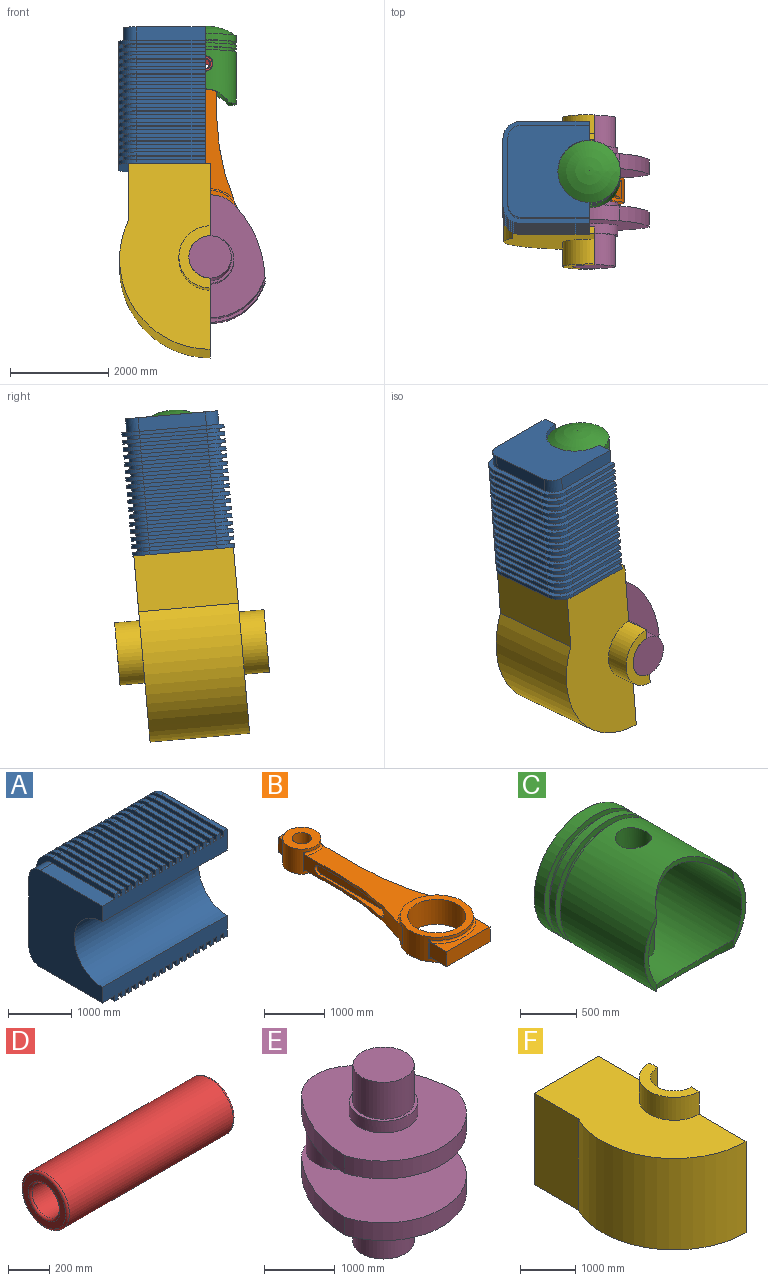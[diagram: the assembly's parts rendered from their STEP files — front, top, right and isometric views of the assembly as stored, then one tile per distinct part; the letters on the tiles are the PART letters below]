
ASSEMBLY  parts=6 mates=6
PART A: 208 faces, bbox 2794x1752.6x2082.8 mm
  f0: plane 1397x279.4mm, normal (0,0,-1), area 390321.8mm2, adj f1,f86,f89,f206
  f1: cylinder r=254mm len=279.4mm, axis (-1,0,0), area 111475.6mm2, adj f0,f2,f89,f206
  f2: plane 1371.6x279.4mm, normal (0,1,0), area 383225mm2, adj f1,f3,f89,f206
  f3: cylinder r=254mm len=279.4mm, axis (-1,0,0), area 111475.6mm2, adj f2,f4,f89,f206
  f4: plane 1397x279.4mm, normal (0,0,1), area 390321.8mm2, adj f3,f87,f89,f206
  f5: plane 1397x76.2mm, normal (0,0,-1), area 106451.4mm2, adj f6,f86,f199,f207
  f6: cylinder r=254mm len=254mm, axis (-1,0,0), area 30402.4mm2, adj f5,f7,f199,f207
  f7: plane 1371.6x76.2mm, normal (0,1,0), area 104515.9mm2, adj f6,f8,f199,f207
  f8: cylinder r=254mm len=254mm, axis (-1,0,0), area 30402.4mm2, adj f7,f9,f199,f207
  f9: plane 1397x76.2mm, normal (0,0,1), area 106451.4mm2, adj f8,f87,f199,f207
  f10: plane 1397x76.2mm, normal (0,0,-1), area 106451.4mm2, adj f11,f86,f192,f200
  f11: cylinder r=254mm len=254mm, axis (-1,0,0), area 30402.4mm2, adj f10,f12,f192,f200
  f12: plane 1371.6x76.2mm, normal (0,1,0), area 104515.9mm2, adj f11,f13,f192,f200
  f13: cylinder r=254mm len=254mm, axis (-1,0,0), area 30402.4mm2, adj f12,f14,f192,f200
  f14: plane 1397x76.2mm, normal (0,0,1), area 106451.4mm2, adj f13,f87,f192,f200
  f15: plane 1397x76.2mm, normal (0,0,-1), area 106451.4mm2, adj f16,f86,f185,f193
  f16: cylinder r=254mm len=254mm, axis (-1,0,0), area 30402.4mm2, adj f15,f17,f185,f193
  f17: plane 1371.6x76.2mm, normal (0,1,0), area 104515.9mm2, adj f16,f18,f185,f193
  f18: cylinder r=254mm len=254mm, axis (-1,0,0), area 30402.4mm2, adj f17,f19,f185,f193
  f19: plane 1397x76.2mm, normal (0,0,1), area 106451.4mm2, adj f18,f87,f185,f193
  f20: plane 1397x76.2mm, normal (0,0,-1), area 106451.4mm2, adj f21,f86,f178,f186
  f21: cylinder r=254mm len=254mm, axis (-1,0,0), area 30402.4mm2, adj f20,f22,f178,f186
  f22: plane 1371.6x76.2mm, normal (0,1,0), area 104515.9mm2, adj f21,f23,f178,f186
  f23: cylinder r=254mm len=254mm, axis (-1,0,0), area 30402.4mm2, adj f22,f24,f178,f186
  f24: plane 1397x76.2mm, normal (0,0,1), area 106451.4mm2, adj f23,f87,f178,f186
  f25: plane 1397x76.2mm, normal (0,0,-1), area 106451.4mm2, adj f26,f86,f171,f179
  f26: cylinder r=254mm len=254mm, axis (-1,0,0), area 30402.4mm2, adj f25,f27,f171,f179
  f27: plane 1371.6x76.2mm, normal (0,1,0), area 104515.9mm2, adj f26,f28,f171,f179
  f28: cylinder r=254mm len=254mm, axis (-1,0,0), area 30402.4mm2, adj f27,f29,f171,f179
  f29: plane 1397x76.2mm, normal (0,0,1), area 106451.4mm2, adj f28,f87,f171,f179
  f30: plane 1397x76.2mm, normal (0,0,-1), area 106451.4mm2, adj f31,f86,f164,f172
  f31: cylinder r=254mm len=254mm, axis (-1,0,0), area 30402.4mm2, adj f30,f32,f164,f172
  f32: plane 1371.6x76.2mm, normal (0,1,0), area 104515.9mm2, adj f31,f33,f164,f172
  f33: cylinder r=254mm len=254mm, axis (-1,0,0), area 30402.4mm2, adj f32,f34,f164,f172
  f34: plane 1397x76.2mm, normal (0,0,1), area 106451.4mm2, adj f33,f87,f164,f172
  f35: plane 1397x76.2mm, normal (0,0,-1), area 106451.4mm2, adj f36,f86,f157,f165
  f36: cylinder r=254mm len=254mm, axis (-1,0,0), area 30402.4mm2, adj f35,f37,f157,f165
  f37: plane 1371.6x76.2mm, normal (0,1,0), area 104515.9mm2, adj f36,f38,f157,f165
  f38: cylinder r=254mm len=254mm, axis (-1,0,0), area 30402.4mm2, adj f37,f39,f157,f165
  f39: plane 1397x76.2mm, normal (0,0,1), area 106451.4mm2, adj f38,f87,f157,f165
  f40: plane 1397x76.2mm, normal (0,0,-1), area 106451.4mm2, adj f41,f86,f150,f158
  f41: cylinder r=254mm len=254mm, axis (-1,0,0), area 30402.4mm2, adj f40,f42,f150,f158
  f42: plane 1371.6x76.2mm, normal (0,1,0), area 104515.9mm2, adj f41,f43,f150,f158
  f43: cylinder r=254mm len=254mm, axis (-1,0,0), area 30402.4mm2, adj f42,f44,f150,f158
  f44: plane 1397x76.2mm, normal (0,0,1), area 106451.4mm2, adj f43,f87,f150,f158
  f45: plane 1397x76.2mm, normal (0,0,-1), area 106451.4mm2, adj f46,f86,f143,f151
  f46: cylinder r=254mm len=254mm, axis (-1,0,0), area 30402.4mm2, adj f45,f47,f143,f151
  f47: plane 1371.6x76.2mm, normal (0,1,0), area 104515.9mm2, adj f46,f48,f143,f151
  f48: cylinder r=254mm len=254mm, axis (-1,0,0), area 30402.4mm2, adj f47,f49,f143,f151
  f49: plane 1397x76.2mm, normal (0,0,1), area 106451.4mm2, adj f48,f87,f143,f151
  f50: plane 1397x76.2mm, normal (0,0,-1), area 106451.4mm2, adj f51,f86,f136,f144
  f51: cylinder r=254mm len=254mm, axis (-1,0,0), area 30402.4mm2, adj f50,f52,f136,f144
  f52: plane 1371.6x76.2mm, normal (0,1,0), area 104515.9mm2, adj f51,f53,f136,f144
  f53: cylinder r=254mm len=254mm, axis (-1,0,0), area 30402.4mm2, adj f52,f54,f136,f144
  f54: plane 1397x76.2mm, normal (0,0,1), area 106451.4mm2, adj f53,f87,f136,f144
  f55: plane 1397x76.2mm, normal (0,0,-1), area 106451.4mm2, adj f56,f86,f129,f137
  f56: cylinder r=254mm len=254mm, axis (-1,0,0), area 30402.4mm2, adj f55,f57,f129,f137
  f57: plane 1371.6x76.2mm, normal (0,1,0), area 104515.9mm2, adj f56,f58,f129,f137
  f58: cylinder r=254mm len=254mm, axis (-1,0,0), area 30402.4mm2, adj f57,f59,f129,f137
  f59: plane 1397x76.2mm, normal (0,0,1), area 106451.4mm2, adj f58,f87,f129,f137
  f60: plane 1397x76.2mm, normal (0,0,-1), area 106451.4mm2, adj f61,f86,f122,f130
  f61: cylinder r=254mm len=254mm, axis (-1,0,0), area 30402.4mm2, adj f60,f62,f122,f130
  f62: plane 1371.6x76.2mm, normal (0,1,0), area 104515.9mm2, adj f61,f63,f122,f130
  f63: cylinder r=254mm len=254mm, axis (-1,0,0), area 30402.4mm2, adj f62,f64,f122,f130
  f64: plane 1397x76.2mm, normal (0,0,1), area 106451.4mm2, adj f63,f87,f122,f130
  f65: plane 1397x76.2mm, normal (0,0,-1), area 106451.4mm2, adj f66,f86,f115,f123
  f66: cylinder r=254mm len=254mm, axis (-1,0,0), area 30402.4mm2, adj f65,f67,f115,f123
  f67: plane 1371.6x76.2mm, normal (0,1,0), area 104515.9mm2, adj f66,f68,f115,f123
  f68: cylinder r=254mm len=254mm, axis (-1,0,0), area 30402.4mm2, adj f67,f69,f115,f123
  f69: plane 1397x76.2mm, normal (0,0,1), area 106451.4mm2, adj f68,f87,f115,f123
  f70: plane 1397x76.2mm, normal (0,0,-1), area 106451.4mm2, adj f71,f86,f108,f116
  f71: cylinder r=254mm len=254mm, axis (-1,0,0), area 30402.4mm2, adj f70,f72,f108,f116
  f72: plane 1371.6x76.2mm, normal (0,1,0), area 104515.9mm2, adj f71,f73,f108,f116
  f73: cylinder r=254mm len=254mm, axis (-1,0,0), area 30402.4mm2, adj f72,f74,f108,f116
  f74: plane 1397x76.2mm, normal (0,0,1), area 106451.4mm2, adj f73,f87,f108,f116
  f75: plane 1397x76.2mm, normal (0,0,-1), area 106451.4mm2, adj f76,f86,f101,f109
  f76: cylinder r=254mm len=254mm, axis (-1,0,0), area 30402.4mm2, adj f75,f77,f101,f109
  f77: plane 1371.6x76.2mm, normal (0,1,0), area 104515.9mm2, adj f76,f78,f101,f109
  f78: cylinder r=254mm len=254mm, axis (-1,0,0), area 30402.4mm2, adj f77,f79,f101,f109
  f79: plane 1397x76.2mm, normal (0,0,1), area 106451.4mm2, adj f78,f87,f101,f109
  f80: plane 1397x76.2mm, normal (0,0,-1), area 106451.4mm2, adj f81,f86,f95,f102
  f81: cylinder r=254mm len=254mm, axis (-1,0,0), area 30402.4mm2, adj f80,f82,f95,f102
  f82: plane 1371.6x76.2mm, normal (0,1,0), area 104515.9mm2, adj f81,f83,f95,f102
  f83: cylinder r=254mm len=254mm, axis (-1,0,0), area 30402.4mm2, adj f82,f84,f95,f102
  f84: plane 1397x76.2mm, normal (0,0,1), area 106451.4mm2, adj f83,f87,f95,f102
  f85: cylinder r=635mm len=2794mm, axis (-1,0,0), area 5573782.3mm2, adj f86,f87,f88,f89
  f86: plane 2794x406.4mm, normal (0,-1,0), area 983223.8mm2, adj f0,f5,f10,f15,f20,f25,f30,f35
  f87: plane 2794x406.4mm, normal (0,-1,0), area 983223.8mm2, adj f4,f9,f14,f19,f24,f29,f34,f39
  f88: plane 2082.8x1752.6mm, normal (1,0,0), area 2962657.5mm2, adj f85,f86,f87,f90,f91,f92,f93,f94
  f89: plane 1879.6x1651mm, normal (-1,0,0), area 2442144.7mm2, adj f0,f1,f2,f3,f4,f85,f86,f87
  f90: plane 1397x76.2mm, normal (0,0,-1), area 106451.4mm2, adj f86,f88,f94,f95
  f91: plane 1397x76.2mm, normal (0,0,1), area 106451.4mm2, adj f87,f88,f92,f95
  f92: cylinder r=355.6mm len=355.6mm, axis (1,0,0), area 42563.4mm2, adj f88,f91,f93,f95
  f93: plane 1371.6x76.2mm, normal (0,1,0), area 104515.9mm2, adj f88,f92,f94,f95
  f94: cylinder r=355.6mm len=355.6mm, axis (1,0,0), area 42563.4mm2, adj f88,f90,f93,f95
  f95: plane 2082.8x1752.6mm, normal (-1,0,0), area 520512.8mm2, adj f80,f81,f82,f83,f84,f86,f87,f90
  f96: plane 1397x76.2mm, normal (0,0,-1), area 106451.4mm2, adj f86,f100,f101,f102
  f97: plane 1397x76.2mm, normal (0,0,1), area 106451.4mm2, adj f87,f98,f101,f102
  f98: cylinder r=355.6mm len=355.6mm, axis (1,0,0), area 42563.4mm2, adj f97,f99,f101,f102
  f99: plane 1371.6x76.2mm, normal (0,1,0), area 104515.9mm2, adj f98,f100,f101,f102
  f100: cylinder r=355.6mm len=355.6mm, axis (1,0,0), area 42563.4mm2, adj f96,f99,f101,f102
  f101: plane 2082.8x1752.6mm, normal (-1,0,0), area 520512.8mm2, adj f75,f76,f77,f78,f79,f86,f87,f96
  f102: plane 2082.8x1752.6mm, normal (1,0,0), area 520512.8mm2, adj f80,f81,f82,f83,f84,f86,f87,f96
  f103: plane 1397x76.2mm, normal (0,0,-1), area 106451.4mm2, adj f86,f107,f108,f109
  f104: plane 1397x76.2mm, normal (0,0,1), area 106451.4mm2, adj f87,f105,f108,f109
  f105: cylinder r=355.6mm len=355.6mm, axis (1,0,0), area 42563.4mm2, adj f104,f106,f108,f109
  f106: plane 1371.6x76.2mm, normal (0,1,0), area 104515.9mm2, adj f105,f107,f108,f109
  f107: cylinder r=355.6mm len=355.6mm, axis (1,0,0), area 42563.4mm2, adj f103,f106,f108,f109
  f108: plane 2082.8x1752.6mm, normal (-1,0,0), area 520512.8mm2, adj f70,f71,f72,f73,f74,f86,f87,f103
  f109: plane 2082.8x1752.6mm, normal (1,0,0), area 520512.8mm2, adj f75,f76,f77,f78,f79,f86,f87,f103
  f110: plane 1397x76.2mm, normal (0,0,-1), area 106451.4mm2, adj f86,f114,f115,f116
  f111: plane 1397x76.2mm, normal (0,0,1), area 106451.4mm2, adj f87,f112,f115,f116
  f112: cylinder r=355.6mm len=355.6mm, axis (1,0,0), area 42563.4mm2, adj f111,f113,f115,f116
  f113: plane 1371.6x76.2mm, normal (0,1,0), area 104515.9mm2, adj f112,f114,f115,f116
  f114: cylinder r=355.6mm len=355.6mm, axis (1,0,0), area 42563.4mm2, adj f110,f113,f115,f116
  f115: plane 2082.8x1752.6mm, normal (-1,0,0), area 520512.8mm2, adj f65,f66,f67,f68,f69,f86,f87,f110
  f116: plane 2082.8x1752.6mm, normal (1,0,0), area 520512.8mm2, adj f70,f71,f72,f73,f74,f86,f87,f110
  f117: plane 1397x76.2mm, normal (0,0,-1), area 106451.4mm2, adj f86,f121,f122,f123
  f118: plane 1397x76.2mm, normal (0,0,1), area 106451.4mm2, adj f87,f119,f122,f123
  f119: cylinder r=355.6mm len=355.6mm, axis (1,0,0), area 42563.4mm2, adj f118,f120,f122,f123
  f120: plane 1371.6x76.2mm, normal (0,1,0), area 104515.9mm2, adj f119,f121,f122,f123
  f121: cylinder r=355.6mm len=355.6mm, axis (1,0,0), area 42563.4mm2, adj f117,f120,f122,f123
  f122: plane 2082.8x1752.6mm, normal (-1,0,0), area 520512.8mm2, adj f60,f61,f62,f63,f64,f86,f87,f117
  f123: plane 2082.8x1752.6mm, normal (1,0,0), area 520512.8mm2, adj f65,f66,f67,f68,f69,f86,f87,f117
  f124: plane 1397x76.2mm, normal (0,0,-1), area 106451.4mm2, adj f86,f128,f129,f130
  f125: plane 1397x76.2mm, normal (0,0,1), area 106451.4mm2, adj f87,f126,f129,f130
  f126: cylinder r=355.6mm len=355.6mm, axis (1,0,0), area 42563.4mm2, adj f125,f127,f129,f130
  f127: plane 1371.6x76.2mm, normal (0,1,0), area 104515.9mm2, adj f126,f128,f129,f130
  f128: cylinder r=355.6mm len=355.6mm, axis (1,0,0), area 42563.4mm2, adj f124,f127,f129,f130
  f129: plane 2082.8x1752.6mm, normal (-1,0,0), area 520512.8mm2, adj f55,f56,f57,f58,f59,f86,f87,f124
  f130: plane 2082.8x1752.6mm, normal (1,0,0), area 520512.8mm2, adj f60,f61,f62,f63,f64,f86,f87,f124
  f131: plane 1397x76.2mm, normal (0,0,-1), area 106451.4mm2, adj f86,f135,f136,f137
  f132: plane 1397x76.2mm, normal (0,0,1), area 106451.4mm2, adj f87,f133,f136,f137
  f133: cylinder r=355.6mm len=355.6mm, axis (1,0,0), area 42563.4mm2, adj f132,f134,f136,f137
  f134: plane 1371.6x76.2mm, normal (0,1,0), area 104515.9mm2, adj f133,f135,f136,f137
  f135: cylinder r=355.6mm len=355.6mm, axis (1,0,0), area 42563.4mm2, adj f131,f134,f136,f137
  f136: plane 2082.8x1752.6mm, normal (-1,0,0), area 520512.8mm2, adj f50,f51,f52,f53,f54,f86,f87,f131
  f137: plane 2082.8x1752.6mm, normal (1,0,0), area 520512.8mm2, adj f55,f56,f57,f58,f59,f86,f87,f131
  f138: plane 1397x76.2mm, normal (0,0,-1), area 106451.4mm2, adj f86,f142,f143,f144
  f139: plane 1397x76.2mm, normal (0,0,1), area 106451.4mm2, adj f87,f140,f143,f144
  f140: cylinder r=355.6mm len=355.6mm, axis (1,0,0), area 42563.4mm2, adj f139,f141,f143,f144
  f141: plane 1371.6x76.2mm, normal (0,1,0), area 104515.9mm2, adj f140,f142,f143,f144
  f142: cylinder r=355.6mm len=355.6mm, axis (1,0,0), area 42563.4mm2, adj f138,f141,f143,f144
  f143: plane 2082.8x1752.6mm, normal (-1,0,0), area 520512.8mm2, adj f45,f46,f47,f48,f49,f86,f87,f138
  f144: plane 2082.8x1752.6mm, normal (1,0,0), area 520512.8mm2, adj f50,f51,f52,f53,f54,f86,f87,f138
  f145: plane 1397x76.2mm, normal (0,0,-1), area 106451.4mm2, adj f86,f149,f150,f151
  f146: plane 1397x76.2mm, normal (0,0,1), area 106451.4mm2, adj f87,f147,f150,f151
  f147: cylinder r=355.6mm len=355.6mm, axis (1,0,0), area 42563.4mm2, adj f146,f148,f150,f151
  f148: plane 1371.6x76.2mm, normal (0,1,0), area 104515.9mm2, adj f147,f149,f150,f151
  f149: cylinder r=355.6mm len=355.6mm, axis (1,0,0), area 42563.4mm2, adj f145,f148,f150,f151
  f150: plane 2082.8x1752.6mm, normal (-1,0,0), area 520512.8mm2, adj f40,f41,f42,f43,f44,f86,f87,f145
  f151: plane 2082.8x1752.6mm, normal (1,0,0), area 520512.8mm2, adj f45,f46,f47,f48,f49,f86,f87,f145
  f152: plane 1397x76.2mm, normal (0,0,-1), area 106451.4mm2, adj f86,f156,f157,f158
  f153: plane 1397x76.2mm, normal (0,0,1), area 106451.4mm2, adj f87,f154,f157,f158
  f154: cylinder r=355.6mm len=355.6mm, axis (1,0,0), area 42563.4mm2, adj f153,f155,f157,f158
  f155: plane 1371.6x76.2mm, normal (0,1,0), area 104515.9mm2, adj f154,f156,f157,f158
  f156: cylinder r=355.6mm len=355.6mm, axis (1,0,0), area 42563.4mm2, adj f152,f155,f157,f158
  f157: plane 2082.8x1752.6mm, normal (-1,0,0), area 520512.8mm2, adj f35,f36,f37,f38,f39,f86,f87,f152
  f158: plane 2082.8x1752.6mm, normal (1,0,0), area 520512.8mm2, adj f40,f41,f42,f43,f44,f86,f87,f152
  f159: plane 1397x76.2mm, normal (0,0,-1), area 106451.4mm2, adj f86,f163,f164,f165
  f160: plane 1397x76.2mm, normal (0,0,1), area 106451.4mm2, adj f87,f161,f164,f165
  f161: cylinder r=355.6mm len=355.6mm, axis (1,0,0), area 42563.4mm2, adj f160,f162,f164,f165
  f162: plane 1371.6x76.2mm, normal (0,1,0), area 104515.9mm2, adj f161,f163,f164,f165
  f163: cylinder r=355.6mm len=355.6mm, axis (1,0,0), area 42563.4mm2, adj f159,f162,f164,f165
  f164: plane 2082.8x1752.6mm, normal (-1,0,0), area 520512.8mm2, adj f30,f31,f32,f33,f34,f86,f87,f159
  f165: plane 2082.8x1752.6mm, normal (1,0,0), area 520512.8mm2, adj f35,f36,f37,f38,f39,f86,f87,f159
  f166: plane 1397x76.2mm, normal (0,0,-1), area 106451.4mm2, adj f86,f170,f171,f172
  f167: plane 1397x76.2mm, normal (0,0,1), area 106451.4mm2, adj f87,f168,f171,f172
  f168: cylinder r=355.6mm len=355.6mm, axis (1,0,0), area 42563.4mm2, adj f167,f169,f171,f172
  f169: plane 1371.6x76.2mm, normal (0,1,0), area 104515.9mm2, adj f168,f170,f171,f172
  f170: cylinder r=355.6mm len=355.6mm, axis (1,0,0), area 42563.4mm2, adj f166,f169,f171,f172
  f171: plane 2082.8x1752.6mm, normal (-1,0,0), area 520512.8mm2, adj f25,f26,f27,f28,f29,f86,f87,f166
  f172: plane 2082.8x1752.6mm, normal (1,0,0), area 520512.8mm2, adj f30,f31,f32,f33,f34,f86,f87,f166
  f173: plane 1397x76.2mm, normal (0,0,-1), area 106451.4mm2, adj f86,f177,f178,f179
  f174: plane 1397x76.2mm, normal (0,0,1), area 106451.4mm2, adj f87,f175,f178,f179
  f175: cylinder r=355.6mm len=355.6mm, axis (1,0,0), area 42563.4mm2, adj f174,f176,f178,f179
  f176: plane 1371.6x76.2mm, normal (0,1,0), area 104515.9mm2, adj f175,f177,f178,f179
  f177: cylinder r=355.6mm len=355.6mm, axis (1,0,0), area 42563.4mm2, adj f173,f176,f178,f179
  f178: plane 2082.8x1752.6mm, normal (-1,0,0), area 520512.8mm2, adj f20,f21,f22,f23,f24,f86,f87,f173
  f179: plane 2082.8x1752.6mm, normal (1,0,0), area 520512.8mm2, adj f25,f26,f27,f28,f29,f86,f87,f173
  f180: plane 1397x76.2mm, normal (0,0,-1), area 106451.4mm2, adj f86,f184,f185,f186
  f181: plane 1397x76.2mm, normal (0,0,1), area 106451.4mm2, adj f87,f182,f185,f186
  f182: cylinder r=355.6mm len=355.6mm, axis (1,0,0), area 42563.4mm2, adj f181,f183,f185,f186
  f183: plane 1371.6x76.2mm, normal (0,1,0), area 104515.9mm2, adj f182,f184,f185,f186
  f184: cylinder r=355.6mm len=355.6mm, axis (1,0,0), area 42563.4mm2, adj f180,f183,f185,f186
  f185: plane 2082.8x1752.6mm, normal (-1,0,0), area 520512.8mm2, adj f15,f16,f17,f18,f19,f86,f87,f180
  f186: plane 2082.8x1752.6mm, normal (1,0,0), area 520512.8mm2, adj f20,f21,f22,f23,f24,f86,f87,f180
  f187: plane 1397x76.2mm, normal (0,0,-1), area 106451.4mm2, adj f86,f191,f192,f193
  f188: plane 1397x76.2mm, normal (0,0,1), area 106451.4mm2, adj f87,f189,f192,f193
  f189: cylinder r=355.6mm len=355.6mm, axis (1,0,0), area 42563.4mm2, adj f188,f190,f192,f193
  f190: plane 1371.6x76.2mm, normal (0,1,0), area 104515.9mm2, adj f189,f191,f192,f193
  f191: cylinder r=355.6mm len=355.6mm, axis (1,0,0), area 42563.4mm2, adj f187,f190,f192,f193
  f192: plane 2082.8x1752.6mm, normal (-1,0,0), area 520512.8mm2, adj f10,f11,f12,f13,f14,f86,f87,f187
  f193: plane 2082.8x1752.6mm, normal (1,0,0), area 520512.8mm2, adj f15,f16,f17,f18,f19,f86,f87,f187
  f194: plane 1397x76.2mm, normal (0,0,-1), area 106451.4mm2, adj f86,f198,f199,f200
  f195: plane 1397x76.2mm, normal (0,0,1), area 106451.4mm2, adj f87,f196,f199,f200
  f196: cylinder r=355.6mm len=355.6mm, axis (1,0,0), area 42563.4mm2, adj f195,f197,f199,f200
  f197: plane 1371.6x76.2mm, normal (0,1,0), area 104515.9mm2, adj f196,f198,f199,f200
  f198: cylinder r=355.6mm len=355.6mm, axis (1,0,0), area 42563.4mm2, adj f194,f197,f199,f200
  f199: plane 2082.8x1752.6mm, normal (-1,0,0), area 520512.8mm2, adj f5,f6,f7,f8,f9,f86,f87,f194
  f200: plane 2082.8x1752.6mm, normal (1,0,0), area 520512.8mm2, adj f10,f11,f12,f13,f14,f86,f87,f194
  f201: plane 1397x76.2mm, normal (0,0,-1), area 106451.4mm2, adj f86,f205,f206,f207
  f202: plane 1397x76.2mm, normal (0,0,1), area 106451.4mm2, adj f87,f203,f206,f207
  f203: cylinder r=355.6mm len=355.6mm, axis (1,0,0), area 42563.4mm2, adj f202,f204,f206,f207
  f204: plane 1371.6x76.2mm, normal (0,1,0), area 104515.9mm2, adj f203,f205,f206,f207
  f205: cylinder r=355.6mm len=355.6mm, axis (1,0,0), area 42563.4mm2, adj f201,f204,f206,f207
  f206: plane 2082.8x1752.6mm, normal (-1,0,0), area 520512.8mm2, adj f0,f1,f2,f3,f4,f86,f87,f201
  f207: plane 2082.8x1752.6mm, normal (1,0,0), area 520512.8mm2, adj f5,f6,f7,f8,f9,f86,f87,f201
PART B: 46 faces, bbox 1349.2x4329.7x508.1 mm
  f0: cylinder r=4709.32mm len=1805.43mm, axis (0,0,-1), area 349864.6mm2, adj f1,f4,f8,f9,f28,f29,f36,f38
  f1: plane 889x381mm, normal (1,0,0), area 154137.5mm2, adj f0,f8,f9,f12,f30,f31,f37,f38
  f2: plane 1219.2x1219.2mm, normal (0,0,1), area 435768.4mm2, adj f4,f5
  f3: plane 1219.2x1219.2mm, normal (0,0,-1), area 435768.4mm2, adj f4,f5
  f4: cylinder r=609.6mm len=1219.2mm, axis (0,0,-1), area 932908.3mm2, adj f0,f2,f3,f7,f24,f25,f26,f27
  f5: cylinder r=482.6mm len=965.2mm, axis (0,0,-1), area 1540390.7mm2, adj f2,f3
  f6: plane 889x381mm, normal (-1,0,0), area 154138.3mm2, adj f7,f8,f9,f12,f30,f31,f41,f42
  f7: cylinder r=4709.32mm len=1805.43mm, axis (0,0,-1), area 349901.4mm2, adj f4,f6,f8,f9,f28,f29,f42,f43
  f8: plane 2454.67x976.49mm, normal (0,0,1), area 1132367.6mm2, adj f0,f1,f6,f7,f29,f30
  f9: plane 2454.67x976.49mm, normal (0,0,-1), area 1132367.6mm2, adj f0,f1,f6,f7,f28,f31
  f10: plane 635x635mm, normal (0,0,1), area 237519.1mm2, adj f12,f13
  f11: plane 635x635mm, normal (0,0,-1), area 237519.1mm2, adj f12,f13
  f12: cylinder r=317.5mm len=635mm, axis (0,0,-1), area 703461.2mm2, adj f1,f6,f10,f11,f30,f31,f32,f33
  f13: cylinder r=158.75mm len=508mm, axis (0,0,-1), area 506707.5mm2, adj f10,f11
  f14: plane 317.5x304.8mm, normal (0,1,0), area 96774mm2, adj f15,f16,f17,f18
  f15: plane 315.74x105.91mm, normal (-1,0,0), area 32331.2mm2, adj f14,f17,f18,f32,f33,f35
  f16: plane 315.74x105.91mm, normal (1,0,0), area 32331.2mm2, adj f14,f17,f18,f32,f34,f35
  f17: plane 317.5x83.77mm, normal (0,0,1), area 18591.5mm2, adj f14,f15,f16,f32
  f18: plane 317.5x83.77mm, normal (0,0,-1), area 18591.5mm2, adj f14,f15,f16,f35
  f19: plane 1016x304.8mm, normal (0,-1,0), area 309676.8mm2, adj f20,f21,f22,f23
  f20: plane 395.1x338.98mm, normal (1,0,0), area 120982.5mm2, adj f19,f22,f23,f25,f26,f27
  f21: plane 395.1x338.98mm, normal (-1,0,0), area 120982.5mm2, adj f19,f22,f23,f24,f25,f26
  f22: plane 1016x341.56mm, normal (0,0,1), area 172913.1mm2, adj f19,f20,f21,f25
  f23: plane 1016x341.56mm, normal (0,0,-1), area 172913.1mm2, adj f19,f20,f21,f26
  f24: cylinder r=38.1mm len=381mm, axis (0,0,-1), area 7772.6mm2, adj f4,f21,f25,f26
  f25: torus R=647.7mm, axis (0,0,1), area 71272.4mm2, adj f4,f20,f21,f22,f24,f27
  f26: torus R=647.7mm, axis (0,0,1), area 71272.6mm2, adj f4,f20,f21,f23,f24,f27
  f27: cylinder r=38.1mm len=381mm, axis (0,0,-1), area 7772.6mm2, adj f4,f20,f25,f26
  f28: torus R=647.7mm, axis (0,0,1), area 74829.5mm2, adj f0,f4,f7,f9
  f29: torus R=647.7mm, axis (0,0,1), area 74829.5mm2, adj f0,f4,f7,f8
  f30: torus R=355.6mm, axis (0,0,1), area 26194.4mm2, adj f1,f6,f8,f12
  f31: torus R=355.6mm, axis (0,0,1), area 26194.3mm2, adj f1,f6,f9,f12
  f32: torus R=355.6mm, axis (0,0,1), area 20359.5mm2, adj f12,f15,f16,f17,f33,f34
  f33: cylinder r=38.1mm len=381mm, axis (0,0,-1), area 12933.1mm2, adj f12,f15,f32,f35
  f34: cylinder r=38.1mm len=381mm, axis (0,0,-1), area 12933.1mm2, adj f12,f16,f32,f35
  f35: torus R=355.6mm, axis (0,0,1), area 20359.5mm2, adj f12,f15,f16,f18,f33,f34
  f36: cylinder r=97.36mm len=194.73mm, axis (-1,0,0), area 56094mm2, adj f0,f38,f39,f40
  f37: cylinder r=97.36mm len=194.73mm, axis (-1,0,0), area 15538.4mm2, adj f1,f38,f39,f40
  f38: plane 1574.8x168.71mm, normal (0,0,-1), area 120949.6mm2, adj f0,f1,f36,f37,f40
  f39: plane 1574.8x168.71mm, normal (0,0,1), area 120949.6mm2, adj f0,f1,f36,f37,f40
  f40: plane 1769.53x194.73mm, normal (1,0,0), area 336435mm2, adj f36,f37,f38,f39
  f41: cylinder r=97.36mm len=194.73mm, axis (1,0,0), area 15538.4mm2, adj f6,f42,f44,f45
  f42: plane 1574.8x168.71mm, normal (0,0,1), area 120949.6mm2, adj f6,f7,f41,f43,f45
  f43: cylinder r=97.36mm len=194.73mm, axis (1,0,0), area 56094.5mm2, adj f7,f42,f44,f45
  f44: plane 1574.8x168.71mm, normal (0,0,-1), area 120949.6mm2, adj f6,f7,f41,f43,f45
  f45: plane 1769.53x194.73mm, normal (-1,0,0), area 336435mm2, adj f41,f42,f43,f44
PART C: 26 faces, bbox 1270x1612.8x1270 mm
  f0: cylinder r=584.2mm len=1168.4mm, axis (0,1,0), area 3086131.1mm2, adj f1,f7,f8,f18,f19,f23,f25
  f1: plane 825.4x152.4mm, normal (0,-1,0), area 40668.5mm2, adj f0,f9,f18,f19
  f2: torus R=24.99mm, axis (0,1,0), area 1403834.6mm2, adj f17
  f3: torus R=24.99mm, axis (0,1,0), area 1178140.1mm2, adj f4
  f4: cylinder r=584.2mm len=1168.4mm, axis (0,1,0), area 185024.3mm2, adj f3,f5
  f5: plane 1168.4x1168.4mm, normal (0,1,0), area 220417.8mm2, adj f4,f6
  f6: cylinder r=520.7mm len=1041.4mm, axis (0,1,0), area 997200.3mm2, adj f5,f7
  f7: plane 1168.4x1168.4mm, normal (0,-1,0), area 220417.8mm2, adj f0,f6
  f8: plane 825.4x152.4mm, normal (0,-1,0), area 40668.5mm2, adj f0,f9,f18,f19
  f9: cylinder r=635mm len=1270mm, axis (0,1,0), area 3672832mm2, adj f1,f8,f10,f18,f19,f20,f21
  f10: plane 1270x1270mm, normal (0,1,0), area 240686.1mm2, adj f9,f11
  f11: cylinder r=571.5mm len=1143mm, axis (0,1,0), area 228018.4mm2, adj f10,f12
  f12: plane 1270x1270mm, normal (0,-1,0), area 240686.1mm2, adj f11,f13
  f13: cylinder r=635mm len=1270mm, axis (0,1,0), area 304024.5mm2, adj f12,f14
  f14: plane 1270x1270mm, normal (0,1,0), area 240686.1mm2, adj f13,f15
  f15: cylinder r=571.5mm len=1143mm, axis (0,1,0), area 228018.4mm2, adj f14,f16
  f16: plane 1270x1270mm, normal (0,-1,0), area 240686.1mm2, adj f15,f17
  f17: cylinder r=635mm len=1270mm, axis (0,1,0), area 506707.5mm2, adj f2,f16
  f18: cylinder r=584.01mm len=965.2mm, axis (0,0,1), area 68239mm2, adj f0,f1,f8,f9
  f19: cylinder r=584.01mm len=965.2mm, axis (0,0,1), area 68242.6mm2, adj f0,f1,f8,f9
  f20: cylinder r=158.75mm len=330.2mm, axis (0,0,1), area 319333.2mm2, adj f9,f22
  f21: cylinder r=158.75mm len=330.2mm, axis (0,0,1), area 319344.2mm2, adj f9,f24
  f22: plane 368.3x368.3mm, normal (0,0,-1), area 27362.2mm2, adj f20,f23
  f23: cylinder r=184.15mm len=368.3mm, axis (0,0,-1), area 306166.9mm2, adj f0,f22
  f24: plane 368.3x368.3mm, normal (0,0,1), area 27362.2mm2, adj f21,f25
  f25: cylinder r=184.15mm len=368.3mm, axis (0,0,1), area 306166.9mm2, adj f0,f24
PART D: 8 faces, bbox 1143x343.7x343.7 mm
  f0: plane 292.1x292.1mm, normal (1,0,0), area 30402.4mm2, adj f6,f7
  f1: plane 292.1x292.1mm, normal (-1,0,0), area 30402.4mm2, adj f4,f5
  f2: cylinder r=158.75mm len=1117.6mm, axis (-1,0,0), area 1114756.5mm2, adj f5,f7
  f3: cylinder r=95.25mm len=1117.6mm, axis (-1,0,0), area 668853.9mm2, adj f4,f6
  f4: torus R=107.95mm, axis (1,0,0), area 12517.5mm2, adj f1,f3
  f5: torus R=146.05mm, axis (1,0,0), area 19319.9mm2, adj f1,f2
  f6: torus R=107.95mm, axis (1,0,0), area 12517.5mm2, adj f0,f3
  f7: torus R=146.05mm, axis (1,0,0), area 19319.9mm2, adj f0,f2
PART E: 21 faces, bbox 2235.2x2509.5x3048 mm
  f0: cylinder r=431.8mm len=863.6mm, axis (0,0,-1), area 1722805.4mm2, adj f1,f3
  f1: plane 863.6x863.6mm, normal (0,0,1), area 585753.8mm2, adj f0
  f2: cylinder r=482.6mm len=965.2mm, axis (0,0,1), area 616156.3mm2, adj f3,f9
  f3: plane 965.2x965.2mm, normal (0,0,1), area 145931.8mm2, adj f0,f2
  f4: cylinder r=2286mm len=1451.93mm, axis (0,0,1), area 488335.1mm2, adj f5,f7,f8,f9
  f5: cylinder r=1168.4mm len=2235.2mm, axis (0,0,1), area 908008.6mm2, adj f4,f6,f8,f9
  f6: cylinder r=2286mm len=1451.93mm, axis (0,0,1), area 488335.1mm2, adj f5,f7,f8,f9
  f7: cylinder r=706.12mm len=1042.85mm, axis (0,0,1), area 357597.9mm2, adj f4,f6,f8,f9
  f8: plane 2509.52x2235.2mm, normal (0,0,-1), area 3466056.1mm2, adj f4,f5,f6,f7,f10
  f9: plane 2509.52x2235.2mm, normal (0,0,1), area 3466056.1mm2, adj f2,f4,f5,f6,f7
  f10: cylinder r=482.6mm len=965.2mm, axis (0,0,1), area 2310586.1mm2, adj f8,f19
  f11: cylinder r=431.8mm len=863.6mm, axis (0,0,1), area 1722805.4mm2, adj f12,f14
  f12: plane 863.6x863.6mm, normal (0,0,-1), area 585753.8mm2, adj f11
  f13: cylinder r=482.6mm len=965.2mm, axis (0,0,-1), area 616156.3mm2, adj f14,f20
  f14: plane 965.2x965.2mm, normal (0,0,-1), area 145931.8mm2, adj f11,f13
  f15: cylinder r=2286mm len=1451.93mm, axis (0,0,-1), area 488335.1mm2, adj f16,f18,f19,f20
  f16: cylinder r=1168.4mm len=2235.2mm, axis (0,0,-1), area 908008.6mm2, adj f15,f17,f19,f20
  f17: cylinder r=2286mm len=1451.93mm, axis (0,0,-1), area 488335.1mm2, adj f16,f18,f19,f20
  f18: cylinder r=706.12mm len=1042.85mm, axis (0,0,-1), area 357597.9mm2, adj f15,f17,f19,f20
  f19: plane 2509.52x2235.2mm, normal (0,0,1), area 3466056.1mm2, adj f10,f15,f16,f17,f18
  f20: plane 2509.52x2235.2mm, normal (0,0,-1), area 3466056.1mm2, adj f13,f15,f16,f17,f18
PART F: 18 faces, bbox 1841.5x3797.3x3048 mm
  f0: plane 3684.35x1728.55mm, normal (0,0,-1), area 5147070.5mm2, adj f2,f3,f4,f8,f10,f11
  f1: cylinder r=635mm len=1270mm, axis (0,0,1), area 1013415mm2, adj f2,f4,f5,f9
  f2: plane 1524x635mm, normal (1,0,0), area 296773.6mm2, adj f0,f1,f3,f5,f8,f9
  f3: cylinder r=431.8mm len=863.6mm, axis (0,0,1), area 861402.7mm2, adj f0,f2,f4,f5
  f4: plane 3048x1409.7mm, normal (1,0,0), area 765333.9mm2, adj f0,f1,f3,f5,f6,f9,f11,f12
  f5: plane 1270x635mm, normal (0,0,1), area 340507.4mm2, adj f1,f2,f3,f4
  f6: cylinder r=1841.5mm len=2657.17mm, axis (0,0,1), area 7594881mm2, adj f4,f7,f9,f17
  f7: plane 2032x1140.13mm, normal (-1,0,0), area 2316739.5mm2, adj f6,f8,f9,f17
  f8: plane 2032x1651mm, normal (0,1,0), area 645160mm2, adj f0,f2,f7,f9,f10,f12,f14,f17
  f9: plane 3797.3x1841.5mm, normal (0,0,1), area 5363734.4mm2, adj f1,f2,f4,f6,f7,f8
  f10: plane 1778x1140.13mm, normal (1,0,0), area 2027147.1mm2, adj f0,f8,f11,f12
  f11: cylinder r=1728.55mm len=2544.23mm, axis (0,0,1), area 6337960.7mm2, adj f0,f4,f10,f12
  f12: plane 3684.35x1728.55mm, normal (0,0,1), area 5147070.5mm2, adj f4,f8,f10,f11,f14,f15
  f13: cylinder r=635mm len=1270mm, axis (0,0,-1), area 1013415mm2, adj f4,f14,f16,f17
  f14: plane 1524x635mm, normal (1,0,0), area 296773.6mm2, adj f8,f12,f13,f15,f16,f17
  f15: cylinder r=431.8mm len=863.6mm, axis (0,0,-1), area 861402.7mm2, adj f4,f12,f14,f16
  f16: plane 1270x635mm, normal (0,0,-1), area 340507.4mm2, adj f4,f13,f14,f15
  f17: plane 3797.3x1841.5mm, normal (0,0,-1), area 5363734.4mm2, adj f4,f6,f7,f8,f13,f14
PLACE A rot(axis=(-0.59,0.59,0.54),122.9deg) t=(-2280.68,2282.24,3547.88)mm
PLACE B rot(axis=(1,-0.02,0.02),85deg) t=(-2179.11,1897.34,-324.59)mm
PLACE C rot(axis=(0,0.74,0.68),180deg) t=(-2280.68,2151.87,2057.75)mm
PLACE D rot(axis=(0.62,0.66,0.43),127.9deg) t=(-2280.68,1649.38,2879.68)mm
PLACE E rot(axis=(1,0,0),85deg) t=(-2179.91,982.65,-1106.36)mm
PLACE F rot(axis=(1,0,0),85deg) t=(-2179.91,856.13,-1095.29)mm fixed
MATE fastened F.f8 <-> A.f88  axis (0,0.09,1) through (-3272.11,2038.72,764.51)mm
MATE cylindrical E.f10 <-> B.f4  axis (0,-1,0.09) through (-2179.11,1943.09,-328.59)mm
MATE slider A.f85 <-> C.f0  axis (0,0.09,1) through (-2280.68,2160.48,2156.2)mm
MATE cylindrical D.f2 <-> B.f12  axis (0,-1,0.09) through (-2280.68,2218.71,2829.87)mm
MATE revolute E.f0 <-> F.f1  axis (0,-1,0.09) through (-2179.91,3070.17,-1289)mm
MATE cylindrical D.f2 <-> C.f20  axis (0,-1,0.09) through (-2280.68,2218.71,2829.87)mm
